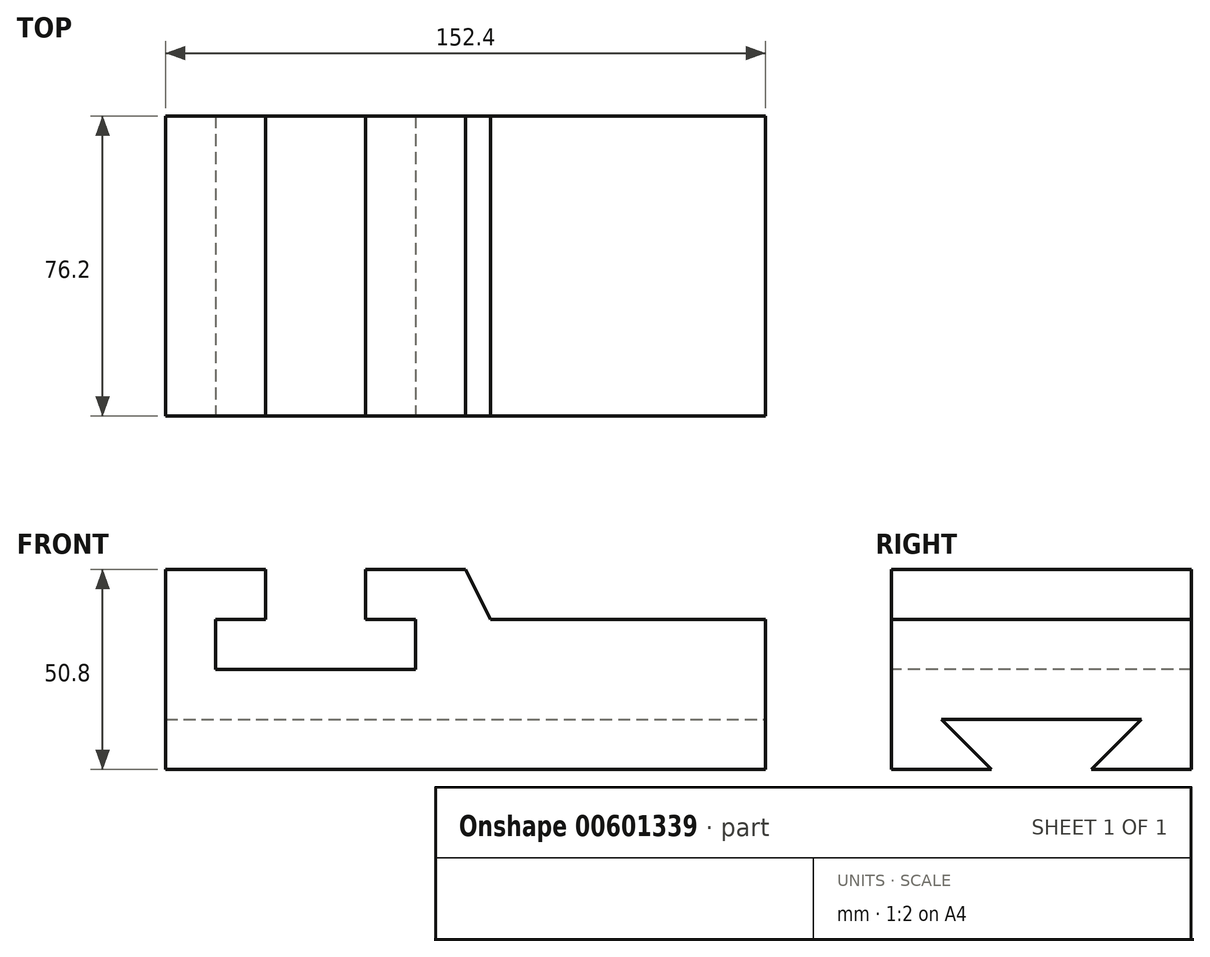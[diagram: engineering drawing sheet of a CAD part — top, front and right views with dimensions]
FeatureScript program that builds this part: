
annotation { "Feature Type Name" : "Feature", "Feature Type Description" : "" }
export const myFeature = defineFeature(function(context is Context, id is Id, definition is map)
    precondition{}
    {
        {
            var Q0;
            Q0=qCreatedBy(makeId("Front.planeOp"),FACE);
            var sketch = newSketch(context, id + "F0", { "sketchPlane" : qUnion([Q0])});
            skLineSegment(sketch, "E0", {"start": v(0, 0) * mm, "end": v(152.4, 0) * mm});
            skLineSegment(sketch, "E1", {"start": v(0, 0) * mm, "end": v(0, 50.8) * mm});
            skLineSegment(sketch, "E2", {"start": v(0, 50.8) * mm, "end": v(25.4, 50.8) * mm});
            skLineSegment(sketch, "E3", {"start": v(25.4, 50.8) * mm, "end": v(25.4, 38.1) * mm});
            skLineSegment(sketch, "E4", {"start": v(25.4, 38.1) * mm, "end": v(12.7, 38.1) * mm});
            skLineSegment(sketch, "E5", {"start": v(12.7, 38.1) * mm, "end": v(12.7, 25.4) * mm});
            skLineSegment(sketch, "E6", {"start": v(12.7, 25.4) * mm, "end": v(63.5, 25.4) * mm});
            skLineSegment(sketch, "E7", {"start": v(63.5, 25.4) * mm, "end": v(63.5, 38.1) * mm});
            skLineSegment(sketch, "E8", {"start": v(63.5, 38.1) * mm, "end": v(50.8, 38.1) * mm});
            skLineSegment(sketch, "E9", {"start": v(50.8, 38.1) * mm, "end": v(50.8, 50.8) * mm});
            skLineSegment(sketch, "E10", {"start": v(50.8, 50.8) * mm, "end": v(76.2, 50.8) * mm});
            skLineSegment(sketch, "E11", {"start": v(76.2, 50.8) * mm, "end": v(82.55, 38.1) * mm});
            skLineSegment(sketch, "E12", {"start": v(82.55, 38.1) * mm, "end": v(152.4, 38.1) * mm});
            skLineSegment(sketch, "E13", {"start": v(152.4, 38.1) * mm, "end": v(152.4, 0) * mm});
            skSolve(sketch);
        }
        {
            var Q0;
            Q0=makeQuery(id+"F0.imprint","IMPRINT",FACE,{"disambiguationData":[TD([[makeQuery(id+"F0.imprint","IMPRINT",EDGE,{"derivedFrom":sQuery(id+"F0.wireOp",EDGE,"E0")}),1.0]])]});
            extrude(context, id + "F1", {"entities" : qUnion([Q0]), "oppositeDirection" : true, "depth" : 76.2 * mm, "offsetDistance" : 25.4 * mm});
        }
        {
            var Q0;
            Q0=makeQuery(id+"F1.opExtrude","SWEPT_FACE",FACE,{"disambiguationData":[OSD([sQuery(id+"F0.wireOp",EDGE,"E13")])]});
            var sketch = newSketch(context, id + "F2", { "sketchPlane" : qUnion([Q0])});
            skLineSegment(sketch, "E14", {"start": v(12.7, 12.7) * mm, "end": v(63.5, 12.7) * mm});
            skLineSegment(sketch, "E15", {"start": v(25.4, 0) * mm, "end": v(12.7, 12.7) * mm});
            skLineSegment(sketch, "E16", {"start": v(50.8, 0) * mm, "end": v(63.5, 12.7) * mm});
            skSolve(sketch);
        }
        {
            var Q0;
            Q0=makeQuery(id+"F2.imprint","IMPRINT",FACE,{"disambiguationData":[TD([[makeQuery(id+"F2.imprint","IMPRINT",EDGE,{"derivedFrom":sQuery(id+"F2.wireOp",EDGE,"E14")}),-1.0]])]});
            extrude(context, id + "F3", {"entities" : qUnion([Q0]), "operationType" : NewBodyOperationType.REMOVE, "oppositeDirection" : true, "depth" : 152.4 * mm, "offsetDistance" : 25.4 * mm});
        }
    });
